# Revit family: BLAUBERG-KOMFORT_EC_SB250
name_source: partatom
category: Mechanical Equipment
units: mm (PartAtom-declared; Revit-internal decimal feet)

## family parameters
Always vertical = Yes
Classification = None
Cut with Voids When Loaded = No
OmniClass Number = 23.75.35.14
OmniClass Title = Air Handling Units
Part Type = Normal
Room Calculation Point = No
Round Connector Dimension = Use Diameter
Shared = No
Work Plane-Based = No

## types (4) — shared parameters
B = 450 mm  [stored 1.47638 ft]
B1 = 123 mm  [stored 0.403543 ft]
B2 = 204 mm  [stored 0.669291 ft]
B3 = 136 mm
BackFeetD = 20 mm  [stored 0.0656168 ft]
Casing Material = Painted Steel White
Current = 1 A
D = 160 mm  [stored 0.524934 ft]
Description = Air Handling Unit
DrainConB = 136 mm
Duct Connection Diameter = 160 mm  [stored 0.524934 ft]
ElBoxA = 85 mm  [stored 0.278871 ft]
ElBoxB = 150 mm
ElConA = 315 mm  [stored 1.03346 ft]
ElConB = 130 mm  [stored 0.426509 ft]
Extract Air Filter = G4
Family Version = 1.0
FilterCoverH = 258 mm  [stored 0.846457 ft]
FilterCoverL = 82 mm  [stored 0.269029 ft]
Front Maintenance Zone Height = 500 mm  [stored 1.64042 ft]
Front Maintenance Zone Length = 567 mm  [stored 1.86024 ft]
Front Maintenance Zone Width = 790 mm  [stored 2.59186 ft]
H = 790 mm  [stored 2.59186 ft]
HDuctCon = 41 mm  [stored 0.134514 ft]
Heat Exchanger Type = counter-flow
L = 567 mm  [stored 1.86024 ft]
L1 = 110 mm  [stored 0.360892 ft]
L2 = 90 mm  [stored 0.295276 ft]
L3 = 110 mm  [stored 0.360892 ft]
Load Classification = HVAC
Maintenance Zone Material = Maintenance Zone
Manufacturer = Blauberg
Maximum Air Flow = 290 m³/h
Maximum Unit Power = 115 W
Metal Material = Metal Zinc
Number of Poles = 1
Plastic Material = Polypropylene Black
Power = 115 W
Power Factor = 1
RPM (min-1) = 2050
SEC Class = A+
ServiceDoorB = 20 mm  [stored 0.0656168 ft]
Sound Pressure Level at 3 m (dBA) = 25
Supply Air Filter = G4,F7
Transported Air Temperature (°C) = -25…+40
URL = https://blaubergventilatoren.de
Unit Current = 1 A
Voltage = 230 V
Weight = 51.00 kg
dBFeets = 78 mm  [stored 0.255906 ft]
dLFeets = 22 mm  [stored 0.0721785 ft]

## per-type parameters (varying)
| type | Drain Connection Diameter | DrainPipe | DrainPipeD | Heat Exchanger Material | Heat recovery efficiency (%) | Type Comments |
| KOMFORT EC SB250 S21 | 18 mm  [stored 0.0590551 ft] | Yes | 18 mm  [stored 0.0590551 ft] | polystyrene | 85..94 | Air Handling Unit KOMFORT EC SB250 S21 |
| KOMFORT EC SB250 S14 | 18 mm  [stored 0.0590551 ft] | Yes | 18 mm  [stored 0.0590551 ft] | polystyrene | 85..94 | Air Handling Unit KOMFORT EC SB250 S14 |
| KOMFORT EC SB250-E S21 | 0 mm  [stored 0 ft] | No | 1 mm  [stored 0.00328084 ft] | enthalpy | 77..90 | Air Handling Unit KOMFORT EC SB250-E S21 |
| KOMFORT EC SB250-E S14 | 0 mm  [stored 0 ft] | No | 1 mm  [stored 0.00328084 ft] | enthalpy | 77..90 | Air Handling Unit KOMFORT EC SB250-E S14 |

note: column(s) folded — value = type name in every type: Model

note: [stored X ft] marks values corroborated as IEEE doubles in the binary element streams (Revit-internal decimal feet)

## geometry (parser evidence)
native form markers: Sweep x7
no freeform markers — native parametric forms only
